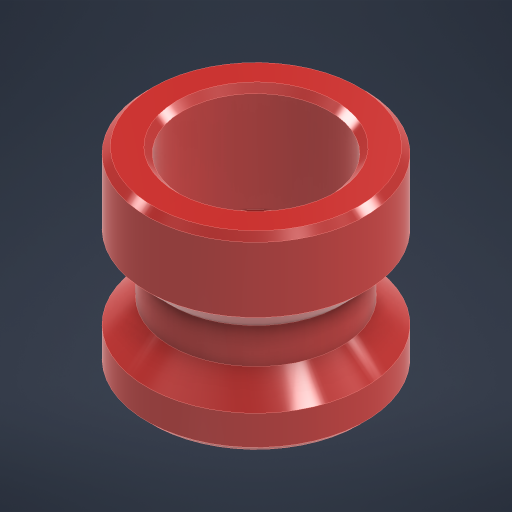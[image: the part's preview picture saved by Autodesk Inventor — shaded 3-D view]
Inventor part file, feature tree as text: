
AUTODESK INVENTOR PART (.ipt)
format: ipt  version: 2025 (Build 290162010, 162A)  size: 265,216 bytes
history: native  units: mm
features: chamfer x2, revolve x1, sketch x1
ambient origin geometry x8: Origin, YZ Plane, XZ Plane, XY Plane, X Axis, Y Axis, Z Axis, Center Point
bodies: Solid1 (feature_tree)
feature tree (4):
  revolve  "Revolution1"  [1 undecoded]
  chamfer  "Chamfer1"  Distance=3.0mm
  chamfer  "Chamfer2"  Distance=3.5mm
  sketch  "Sketch1"  dims[d0=1.6mm d1=8.0mm d2=3.0mm d3=3.5mm d4=1.5mm d5=4.0mm d6=1.0mm d7=1.5mm d8=360.0deg d9=1.0mm d10=2.0mm d11=45.0deg d12=0.25mm d13=2.0mm d14=45.0deg]
note: 1 required parameter value undecoded (feature->parameter linkage not recoverable at this tier; creation-order binding heuristic only, values carry confidence <= 0.55)
